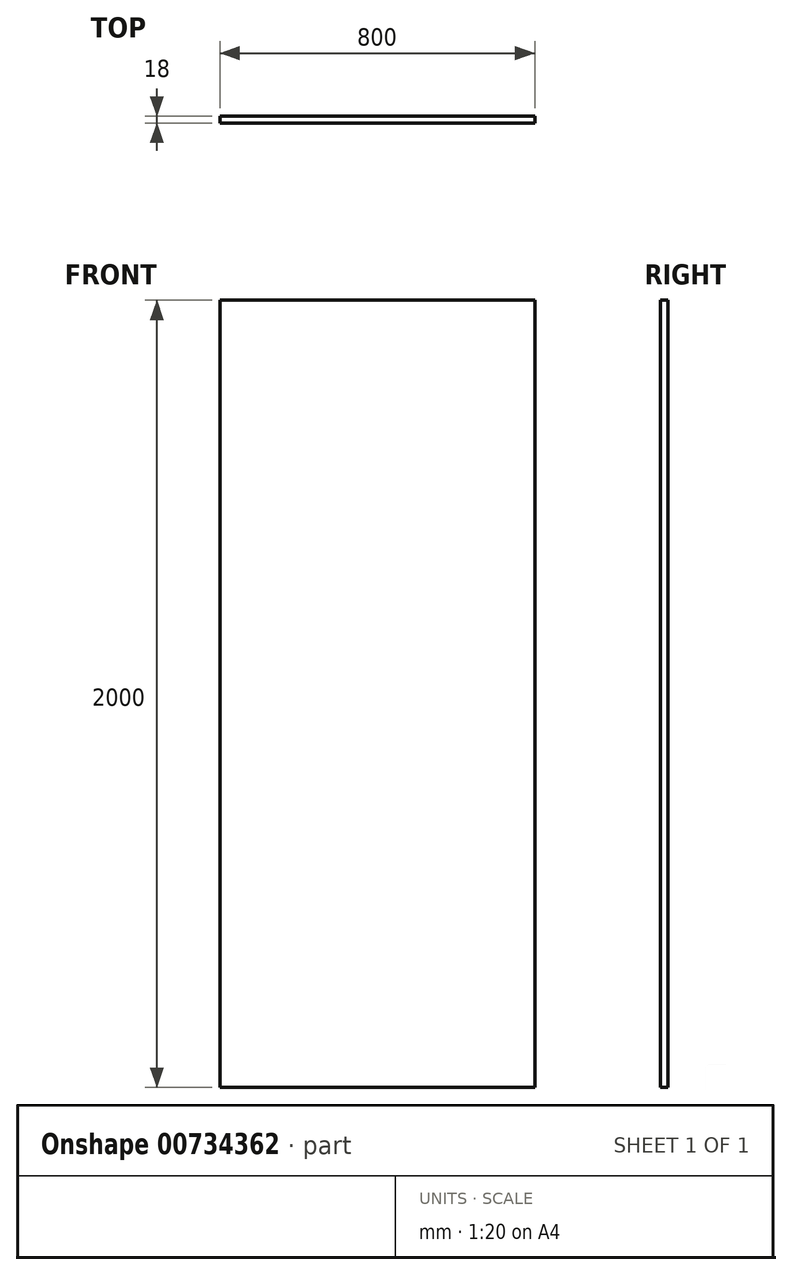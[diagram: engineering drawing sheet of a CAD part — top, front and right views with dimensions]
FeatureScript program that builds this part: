
annotation { "Feature Type Name" : "Feature", "Feature Type Description" : "" }
export const myFeature = defineFeature(function(context is Context, id is Id, definition is map)
    precondition{}
    {
        {
            var Q0;
            Q0=qCreatedBy(makeId("Front.planeOp"),FACE);
            var sketch = newSketch(context, id + "F0", { "sketchPlane" : qUnion([Q0])});
            skLineSegment(sketch, "E0.bottom", {"start": v(-400, -1000) * mm, "end": v(400, -1000) * mm});
            skLineSegment(sketch, "E0.top", {"start": v(-400, 1000) * mm, "end": v(400, 1000) * mm});
            skLineSegment(sketch, "E0.left", {"start": v(-400, -1000) * mm, "end": v(-400, 1000) * mm});
            skLineSegment(sketch, "E0.right", {"start": v(400, -1000) * mm, "end": v(400, 1000) * mm});
            skPoint(sketch, "E0.middle", {"position": v(0, 0) * mm});
            skSolve(sketch);
        }
        {
            var Q0;
            Q0 = qSketchRegion(id + "F0", true);
            extrude(context, id + "F1", {"entities" : qUnion([Q0]), "oppositeDirection" : true, "depth" : 18 * mm, "offsetDistance" : 25 * mm});
        }
    });
